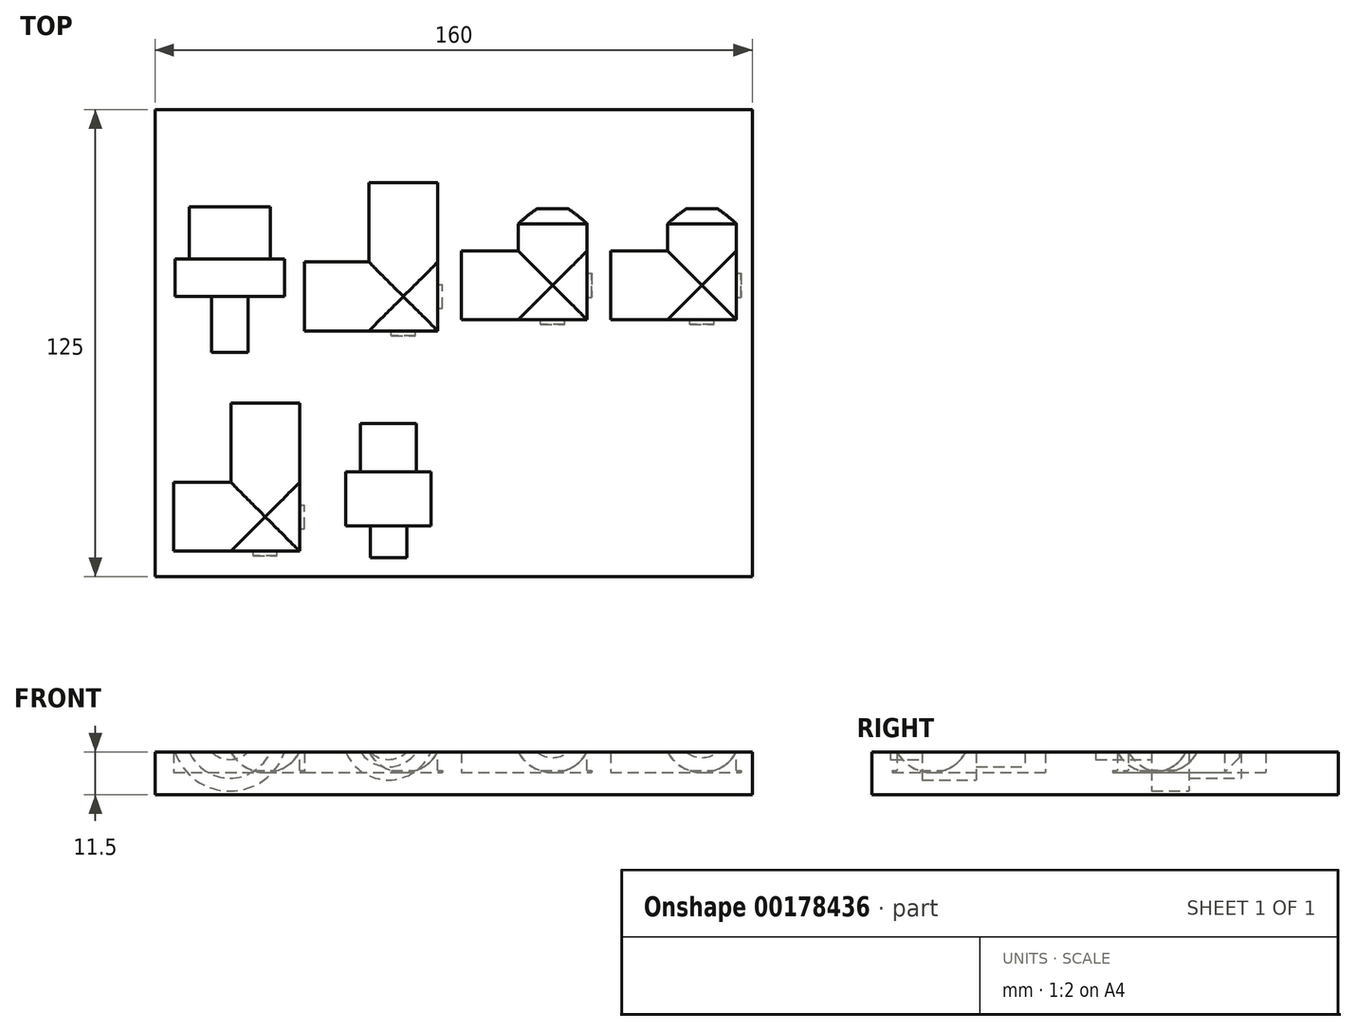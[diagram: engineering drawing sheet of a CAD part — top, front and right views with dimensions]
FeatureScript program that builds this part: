
annotation { "Feature Type Name" : "Feature", "Feature Type Description" : "" }
export const myFeature = defineFeature(function(context is Context, id is Id, definition is map)
    precondition{}
    {
        {
            var Q0;
            Q0=qCreatedBy(makeId("Top.planeOp"),FACE);
            var sketch = newSketch(context, id + "F0", { "sketchPlane" : qUnion([Q0])});
            skLineSegment(sketch, "E0.bottom", {"start": v(0, 0) * mm, "end": v(160, 0) * mm});
            skLineSegment(sketch, "E0.top", {"start": v(0, 125) * mm, "end": v(160, 125) * mm});
            skLineSegment(sketch, "E0.left", {"start": v(0, 0) * mm, "end": v(0, 125) * mm});
            skLineSegment(sketch, "E0.right", {"start": v(160, 0) * mm, "end": v(160, 125) * mm});
            skSolve(sketch);
        }
        {
            var Q0;
            Q0=makeQuery(id+"F0.imprint","IMPRINT",FACE,{"disambiguationData":[TD([[makeQuery(id+"F0.imprint","IMPRINT",EDGE,{"derivedFrom":sQuery(id+"F0.wireOp",EDGE,"E0.bottom")}),1.0]])]});
            extrude(context, id + "F1", {"entities" : qUnion([Q0]), "oppositeDirection" : true, "depth" : 16.5 * mm});
        }
        {
            var Q0;
            Q0=makeQuery(id+"F1.opExtrude","CAP_FACE",FACE,{"disambiguationData":[OSD([sQuery(id+"F0.wireOp",EDGE,"E0.bottom"),sQuery(id+"F0.wireOp",EDGE,"E0.top"),sQuery(id+"F0.wireOp",EDGE,"E0.left"),sQuery(id+"F0.wireOp",EDGE,"E0.right")])],"isStart":true});
            var sketch = newSketch(context, id + "F2", { "sketchPlane" : qUnion([Q0])});
            skLineSegment(sketch, "E1.bottom", {"start": v(0, 0) * mm, "end": v(20, 0) * mm, "construction": true});
            skLineSegment(sketch, "E1.top", {"start": v(0, 60) * mm, "end": v(20, 60) * mm, "construction": true});
            skLineSegment(sketch, "E1.left", {"start": v(0, 0) * mm, "end": v(0, 60) * mm, "construction": true});
            skLineSegment(sketch, "E1.right", {"start": v(20, 0) * mm, "end": v(20, 60) * mm, "construction": true});
            skLineSegment(sketch, "E2.bottom", {"start": v(20, 60) * mm, "end": v(27, 60) * mm});
            skLineSegment(sketch, "E2.left", {"start": v(20, 60) * mm, "end": v(20, 75) * mm});
            skLineSegment(sketch, "E2.right", {"start": v(27, 60) * mm, "end": v(27, 75) * mm});
            skLineSegment(sketch, "E3.bottom", {"start": v(27, 75) * mm, "end": v(35.5, 75) * mm});
            skLineSegment(sketch, "E3.top", {"start": v(32, 85) * mm, "end": v(35.5, 85) * mm});
            skLineSegment(sketch, "E3.left", {"start": v(20, 75) * mm, "end": v(20, 85) * mm});
            skLineSegment(sketch, "E3.right", {"start": v(35.5, 75) * mm, "end": v(35.5, 85) * mm});
            skLineSegment(sketch, "E4.top", {"start": v(24.5, 99) * mm, "end": v(32, 99) * mm});
            skLineSegment(sketch, "E4.left", {"start": v(20, 85) * mm, "end": v(20, 99) * mm});
            skLineSegment(sketch, "E4.right", {"start": v(32, 85) * mm, "end": v(32, 99) * mm});
            skLineSegment(sketch, "E5.top", {"start": v(20, 113) * mm, "end": v(24.5, 113) * mm});
            skLineSegment(sketch, "E5.left", {"start": v(20, 99) * mm, "end": v(20, 113) * mm});
            skLineSegment(sketch, "E5.right", {"start": v(24.5, 99) * mm, "end": v(24.5, 113) * mm});
            skSolve(sketch);
        }
        {
            var Q0;
            Q0=qSketchRegion(id+"F2",true);
            var Q1;
            Q1=sQuery(id+"F2.wireOp",EDGE,"E4.left");
            revolve(context, id + "F3", {"operationType" : NewBodyOperationType.REMOVE, "entities" : qUnion([Q0]), "axis" : qUnion([Q1]), "revolveType" : RevolveType.FULL, "oppositeDirection" : true});
        }
        {
            var Q0;
            Q0=makeQuery(id+"F1.opExtrude","CAP_FACE",FACE,{"disambiguationData":[OSD([sQuery(id+"F0.wireOp",EDGE,"E0.bottom"),sQuery(id+"F0.wireOp",EDGE,"E0.top"),sQuery(id+"F0.wireOp",EDGE,"E0.left"),sQuery(id+"F0.wireOp",EDGE,"E0.right")])],"isStart":true});
            var sketch = newSketch(context, id + "F4", { "sketchPlane" : qUnion([Q0])});
            skLineSegment(sketch, "E6.bottom", {"start": v(0, 0) * mm, "end": v(5, 0) * mm, "construction": true});
            skLineSegment(sketch, "E6.top", {"start": v(0, 16) * mm, "end": v(5, 16) * mm, "construction": true});
            skLineSegment(sketch, "E6.left", {"start": v(0, 0) * mm, "end": v(0, 16) * mm, "construction": true});
            skLineSegment(sketch, "E6.right", {"start": v(5, 0) * mm, "end": v(5, 16) * mm, "construction": true});
            skLineSegment(sketch, "E7.bottom", {"start": v(5, 16) * mm, "end": v(40, 16) * mm});
            skLineSegment(sketch, "E7.top", {"start": v(5, 5.5) * mm, "end": v(40, 5.5) * mm});
            skLineSegment(sketch, "E7.left", {"start": v(5, 16) * mm, "end": v(5, 5.5) * mm});
            skLineSegment(sketch, "E7.right", {"start": v(40, 16) * mm, "end": v(40, 5.5) * mm});
            skSolve(sketch);
        }
        {
            var Q0;
            Q0=makeQuery(id+"F4.imprint","IMPRINT",FACE,{"disambiguationData":[TD([[makeQuery(id+"F4.imprint","IMPRINT",EDGE,{"derivedFrom":sQuery(id+"F4.wireOp",EDGE,"E7.bottom")}),-1.0]])]});
            var Q1;
            Q1=sQuery(id+"F4.wireOp",EDGE,"E7.bottom");
            revolve(context, id + "F5", {"operationType" : NewBodyOperationType.REMOVE, "entities" : qUnion([Q0]), "axis" : qUnion([Q1]), "revolveType" : RevolveType.FULL, "oppositeDirection" : true});
        }
        {
            var Q0;
            Q0=makeQuery(id+"F1.opExtrude","CAP_FACE",FACE,{"disambiguationData":[OSD([sQuery(id+"F0.wireOp",EDGE,"E0.bottom"),sQuery(id+"F0.wireOp",EDGE,"E0.top"),sQuery(id+"F0.wireOp",EDGE,"E0.left"),sQuery(id+"F0.wireOp",EDGE,"E0.right")])],"isStart":true});
            var sketch = newSketch(context, id + "F6", { "sketchPlane" : qUnion([Q0])});
            skLineSegment(sketch, "E8.bottom", {"start": v(0, 0) * mm, "end": v(40, 0) * mm, "construction": true});
            skLineSegment(sketch, "E8.top", {"start": v(0, 75) * mm, "end": v(40, 75) * mm, "construction": true});
            skLineSegment(sketch, "E8.left", {"start": v(0, 0) * mm, "end": v(0, 75) * mm, "construction": true});
            skLineSegment(sketch, "E8.right", {"start": v(40, 0) * mm, "end": v(40, 75) * mm, "construction": true});
            skPoint(sketch, "E9.oppositeSnap0", {"position": v(31, 64.5) * mm});
            skLineSegment(sketch, "E9.bottom", {"start": v(40, 75) * mm, "end": v(77, 75) * mm});
            skLineSegment(sketch, "E9.top", {"start": v(40, 64.5) * mm, "end": v(77, 64.5) * mm});
            skLineSegment(sketch, "E9.left", {"start": v(40, 75) * mm, "end": v(40, 64.5) * mm});
            skLineSegment(sketch, "E9.right", {"start": v(77, 75) * mm, "end": v(77, 64.5) * mm});
            skSolve(sketch);
        }
        {
            var Q0;
            Q0=makeQuery(id+"F6.imprint","IMPRINT",FACE,{"disambiguationData":[TD([[makeQuery(id+"F6.imprint","IMPRINT",EDGE,{"derivedFrom":sQuery(id+"F6.wireOp",EDGE,"E9.bottom")}),-1.0]])]});
            var Q1;
            Q1=sQuery(id+"F6.wireOp",EDGE,"E9.bottom");
            revolve(context, id + "F7", {"operationType" : NewBodyOperationType.REMOVE, "entities" : qUnion([Q0]), "axis" : qUnion([Q1]), "revolveType" : RevolveType.FULL, "oppositeDirection" : true});
        }
        {
            var Q0;
            Q0=makeQuery(id+"F1.opExtrude","CAP_FACE",FACE,{"disambiguationData":[OSD([sQuery(id+"F0.wireOp",EDGE,"E0.bottom"),sQuery(id+"F0.wireOp",EDGE,"E0.top"),sQuery(id+"F0.wireOp",EDGE,"E0.left"),sQuery(id+"F0.wireOp",EDGE,"E0.right")])],"isStart":true});
            var sketch = newSketch(context, id + "F8", { "sketchPlane" : qUnion([Q0])});
            skLineSegment(sketch, "E10.bottom", {"start": v(77, 64.5) * mm, "end": v(66.5, 64.5) * mm});
            skLineSegment(sketch, "E10.top", {"start": v(77, 105.5) * mm, "end": v(66.5, 105.5) * mm});
            skLineSegment(sketch, "E10.left", {"start": v(77, 64.5) * mm, "end": v(77, 105.5) * mm});
            skLineSegment(sketch, "E10.right", {"start": v(66.5, 64.5) * mm, "end": v(66.5, 105.5) * mm});
            skSolve(sketch);
        }
        {
            var Q0;
            {var subQ0=sQuery(id+"F8.wireOp",EDGE,"E10.top");Q0=makeQuery(id+"F8.imprint","IMPRINT",FACE,{"disambiguationData":[TD([[makeQuery(id+"F8.imprint","IMPRINT",EDGE,{"derivedFrom":subQ0}),1.0]])]});}
            var Q1;
            {var subQ0=sQuery(id+"F8.wireOp",EDGE,"E10.bottom");Q1=makeQuery(id+"F8.imprint","IMPRINT",FACE,{"disambiguationData":[TD([[makeQuery(id+"F8.imprint","IMPRINT",EDGE,{"derivedFrom":subQ0}),-1.0]])]});}
            var Q2;
            Q2=sQuery(id+"F8.wireOp",EDGE,"E10.right");
            revolve(context, id + "F9", {"operationType" : NewBodyOperationType.REMOVE, "entities" : qUnion([Q0, Q1]), "axis" : qUnion([Q2]), "revolveType" : RevolveType.FULL, "oppositeDirection" : true});
        }
        {
            var Q0;
            Q0=makeQuery(id+"F1.opExtrude","CAP_FACE",FACE,{"disambiguationData":[OSD([sQuery(id+"F0.wireOp",EDGE,"E0.bottom"),sQuery(id+"F0.wireOp",EDGE,"E0.top"),sQuery(id+"F0.wireOp",EDGE,"E0.left"),sQuery(id+"F0.wireOp",EDGE,"E0.right")])],"isStart":true});
            var sketch = newSketch(context, id + "F10", { "sketchPlane" : qUnion([Q0])});
            skLineSegment(sketch, "E11.bottom", {"start": v(77, 64.5) * mm, "end": v(82, 64.5) * mm, "construction": true});
            skLineSegment(sketch, "E11.top", {"start": v(77, 67.5) * mm, "end": v(82, 67.5) * mm, "construction": true});
            skLineSegment(sketch, "E11.left", {"start": v(77, 64.5) * mm, "end": v(77, 67.5) * mm, "construction": true});
            skLineSegment(sketch, "E11.right", {"start": v(82, 64.5) * mm, "end": v(82, 67.5) * mm, "construction": true});
            skLineSegment(sketch, "E12.bottom", {"start": v(82, 67.5) * mm, "end": v(117, 67.5) * mm});
            skLineSegment(sketch, "E12.top", {"start": v(82, 78) * mm, "end": v(117, 78) * mm});
            skLineSegment(sketch, "E12.left", {"start": v(82, 67.5) * mm, "end": v(82, 78) * mm});
            skLineSegment(sketch, "E12.right", {"start": v(117, 67.5) * mm, "end": v(117, 78) * mm});
            skLineSegment(sketch, "E13", {"start": v(117, 67.5) * mm, "end": v(122, 67.5) * mm, "construction": true});
            skLineSegment(sketch, "E14.bottom", {"start": v(122, 67.5) * mm, "end": v(157, 67.5) * mm});
            skLineSegment(sketch, "E14.top", {"start": v(122, 78) * mm, "end": v(157, 78) * mm});
            skLineSegment(sketch, "E14.left", {"start": v(122, 67.5) * mm, "end": v(122, 78) * mm});
            skLineSegment(sketch, "E14.right", {"start": v(157, 67.5) * mm, "end": v(157, 78) * mm});
            skSolve(sketch);
        }
        {
            var Q0;
            Q0=makeQuery(id+"F10.imprint","IMPRINT",FACE,{"disambiguationData":[TD([[makeQuery(id+"F10.imprint","IMPRINT",EDGE,{"derivedFrom":sQuery(id+"F10.wireOp",EDGE,"E12.bottom")}),1.0]])]});
            var Q1;
            Q1=makeQuery(id+"F10.imprint","IMPRINT",FACE,{"disambiguationData":[TD([[makeQuery(id+"F10.imprint","IMPRINT",EDGE,{"derivedFrom":sQuery(id+"F10.wireOp",EDGE,"E14.bottom")}),1.0]])]});
            var Q2;
            Q2=sQuery(id+"F10.wireOp",EDGE,"E12.top");
            revolve(context, id + "F11", {"operationType" : NewBodyOperationType.REMOVE, "entities" : qUnion([Q0, Q1]), "axis" : qUnion([Q2]), "revolveType" : RevolveType.FULL, "oppositeDirection" : true});
        }
        {
            var Q0;
            Q0=makeQuery(id+"F1.opExtrude","CAP_FACE",FACE,{"disambiguationData":[OSD([sQuery(id+"F0.wireOp",EDGE,"E0.bottom"),sQuery(id+"F0.wireOp",EDGE,"E0.top"),sQuery(id+"F0.wireOp",EDGE,"E0.left"),sQuery(id+"F0.wireOp",EDGE,"E0.right")])],"isStart":true});
            var sketch = newSketch(context, id + "F12", { "sketchPlane" : qUnion([Q0])});
            skLineSegment(sketch, "E15.bottom", {"start": v(117, 67.5) * mm, "end": v(106.5, 67.5) * mm});
            skLineSegment(sketch, "E15.top", {"start": v(113, 98.5) * mm, "end": v(106.5, 98.5) * mm});
            skLineSegment(sketch, "E15.left", {"start": v(117, 67.5) * mm, "end": v(117, 94.5) * mm});
            skLineSegment(sketch, "E15.right", {"start": v(106.5, 67.5) * mm, "end": v(106.5, 98.5) * mm});
            skLineSegment(sketch, "E16", {"start": v(117, 67.5) * mm, "end": v(117, 94.5) * mm, "construction": true});
            skLineSegment(sketch, "E17", {"start": v(117, 94.5) * mm, "end": v(113, 98.5) * mm});
            skSolve(sketch);
        }
        {
            var Q0;
            {var subQ5=sQuery(id+"F12.wireOp",EDGE,"E15.top");Q0=makeQuery(id+"F12.imprint","IMPRINT",FACE,{"disambiguationData":[TD([[makeQuery(id+"F12.imprint","IMPRINT",EDGE,{"derivedFrom":subQ5}),1.0]])]});}
            var Q1;
            {var subQ0=sQuery(id+"F12.wireOp",EDGE,"E15.bottom");Q1=makeQuery(id+"F12.imprint","IMPRINT",FACE,{"disambiguationData":[TD([[makeQuery(id+"F12.imprint","IMPRINT",EDGE,{"derivedFrom":subQ0}),-1.0]])]});}
            var Q2;
            Q2=sQuery(id+"F12.wireOp",EDGE,"E15.right");
            revolve(context, id + "F13", {"operationType" : NewBodyOperationType.REMOVE, "entities" : qUnion([Q0, Q1]), "axis" : qUnion([Q2]), "revolveType" : RevolveType.FULL, "oppositeDirection" : true});
        }
        {
            var Q0;
            Q0=makeQuery(id+"F1.opExtrude","CAP_FACE",FACE,{"disambiguationData":[OSD([sQuery(id+"F0.wireOp",EDGE,"E0.bottom"),sQuery(id+"F0.wireOp",EDGE,"E0.top"),sQuery(id+"F0.wireOp",EDGE,"E0.left"),sQuery(id+"F0.wireOp",EDGE,"E0.right")])],"isStart":true});
            var sketch = newSketch(context, id + "F14", { "sketchPlane" : qUnion([Q0])});
            skLineSegment(sketch, "E18.bottom", {"start": v(157, 67.5) * mm, "end": v(146.5, 67.5) * mm});
            skLineSegment(sketch, "E18.top", {"start": v(153, 98.5) * mm, "end": v(146.5, 98.5) * mm});
            skLineSegment(sketch, "E18.left", {"start": v(157, 67.5) * mm, "end": v(157, 94.5) * mm});
            skLineSegment(sketch, "E18.right", {"start": v(146.5, 67.5) * mm, "end": v(146.5, 98.5) * mm});
            skLineSegment(sketch, "E19", {"start": v(157, 67.5) * mm, "end": v(157, 94.5) * mm, "construction": true});
            skLineSegment(sketch, "E20", {"start": v(157, 94.5) * mm, "end": v(153, 98.5) * mm});
            skSolve(sketch);
        }
        {
            var Q0;
            {var subQ2=sQuery(id+"F14.wireOp",EDGE,"E18.top");Q0=makeQuery(id+"F14.imprint","IMPRINT",FACE,{"disambiguationData":[TD([[makeQuery(id+"F14.imprint","IMPRINT",EDGE,{"derivedFrom":subQ2}),1.0]])]});}
            var Q1;
            {var subQ0=sQuery(id+"F14.wireOp",EDGE,"E18.bottom");Q1=makeQuery(id+"F14.imprint","IMPRINT",FACE,{"disambiguationData":[TD([[makeQuery(id+"F14.imprint","IMPRINT",EDGE,{"derivedFrom":subQ0}),-1.0]])]});}
            var Q2;
            Q2=sQuery(id+"F14.wireOp",EDGE,"E18.right");
            revolve(context, id + "F15", {"operationType" : NewBodyOperationType.REMOVE, "entities" : qUnion([Q0, Q1]), "axis" : qUnion([Q2]), "revolveType" : RevolveType.FULL, "oppositeDirection" : true});
        }
        {
            var Q0;
            Q0=makeQuery(id+"F1.opExtrude","CAP_FACE",FACE,{"disambiguationData":[OSD([sQuery(id+"F0.wireOp",EDGE,"E0.bottom"),sQuery(id+"F0.wireOp",EDGE,"E0.top"),sQuery(id+"F0.wireOp",EDGE,"E0.left"),sQuery(id+"F0.wireOp",EDGE,"E0.right")])],"isStart":true});
            var sketch = newSketch(context, id + "F16", { "sketchPlane" : qUnion([Q0])});
            skLineSegment(sketch, "E21.bottom", {"start": v(40, 5.5) * mm, "end": v(29.5, 5.5) * mm});
            skLineSegment(sketch, "E21.top", {"start": v(40, 46.5) * mm, "end": v(29.5, 46.5) * mm});
            skLineSegment(sketch, "E21.left", {"start": v(40, 5.5) * mm, "end": v(40, 46.5) * mm});
            skLineSegment(sketch, "E21.right", {"start": v(29.5, 5.5) * mm, "end": v(29.5, 46.5) * mm});
            skSolve(sketch);
        }
        {
            var Q0;
            {var subQ0=sQuery(id+"F16.wireOp",EDGE,"E21.top");Q0=makeQuery(id+"F16.imprint","IMPRINT",FACE,{"disambiguationData":[TD([[makeQuery(id+"F16.imprint","IMPRINT",EDGE,{"derivedFrom":subQ0}),1.0]])]});}
            var Q1;
            {var subQ0=sQuery(id+"F16.wireOp",EDGE,"E21.bottom");Q1=makeQuery(id+"F16.imprint","IMPRINT",FACE,{"disambiguationData":[TD([[makeQuery(id+"F16.imprint","IMPRINT",EDGE,{"derivedFrom":subQ0}),-1.0]])]});}
            var Q2;
            Q2=sQuery(id+"F16.wireOp",EDGE,"E21.right");
            revolve(context, id + "F17", {"operationType" : NewBodyOperationType.REMOVE, "entities" : qUnion([Q0, Q1]), "axis" : qUnion([Q2]), "revolveType" : RevolveType.FULL, "oppositeDirection" : true});
        }
        {
            var Q0;
            Q0=makeQuery(id+"F1.opExtrude","CAP_FACE",FACE,{"disambiguationData":[OSD([sQuery(id+"F0.wireOp",EDGE,"E0.bottom"),sQuery(id+"F0.wireOp",EDGE,"E0.top"),sQuery(id+"F0.wireOp",EDGE,"E0.left"),sQuery(id+"F0.wireOp",EDGE,"E0.right")])],"isStart":true});
            var sketch = newSketch(context, id + "F18", { "sketchPlane" : qUnion([Q0])});
            skLineSegment(sketch, "E22.bottom", {"start": v(0, 0) * mm, "end": v(62.5, 0) * mm, "construction": true});
            skLineSegment(sketch, "E22.top", {"start": v(0, 5) * mm, "end": v(62.5, 5) * mm, "construction": true});
            skLineSegment(sketch, "E22.left", {"start": v(0, 0) * mm, "end": v(0, 5) * mm, "construction": true});
            skLineSegment(sketch, "E22.right", {"start": v(62.5, 0) * mm, "end": v(62.5, 5) * mm, "construction": true});
            skLineSegment(sketch, "E23.bottom", {"start": v(62.5, 5) * mm, "end": v(69.5, 5) * mm});
            skLineSegment(sketch, "E23.left", {"start": v(62.5, 5) * mm, "end": v(62.5, 13.5) * mm});
            skLineSegment(sketch, "E23.right", {"start": v(69.5, 5) * mm, "end": v(69.5, 13.5) * mm});
            skLineSegment(sketch, "E24.bottom", {"start": v(69.5, 13.5) * mm, "end": v(75, 13.5) * mm});
            skLineSegment(sketch, "E24.top", {"start": v(71.5, 28) * mm, "end": v(75, 28) * mm});
            skLineSegment(sketch, "E24.left", {"start": v(62.5, 13.5) * mm, "end": v(62.5, 28) * mm});
            skLineSegment(sketch, "E24.right", {"start": v(75, 13.5) * mm, "end": v(75, 28) * mm});
            skLineSegment(sketch, "E25.top", {"start": v(62.5, 41) * mm, "end": v(71.5, 41) * mm});
            skLineSegment(sketch, "E25.left", {"start": v(62.5, 28) * mm, "end": v(62.5, 41) * mm});
            skLineSegment(sketch, "E25.right", {"start": v(71.5, 28) * mm, "end": v(71.5, 41) * mm});
            skSolve(sketch);
        }
        {
            var Q0;
            Q0=makeQuery(id+"F18.imprint","IMPRINT",FACE,{"disambiguationData":[TD([[makeQuery(id+"F18.imprint","IMPRINT",EDGE,{"derivedFrom":sQuery(id+"F18.wireOp",EDGE,"E23.bottom")}),1.0]])]});
            var Q1;
            Q1=sQuery(id+"F18.wireOp",EDGE,"E24.left");
            revolve(context, id + "F19", {"operationType" : NewBodyOperationType.REMOVE, "entities" : qUnion([Q0]), "axis" : qUnion([Q1]), "revolveType" : RevolveType.FULL, "oppositeDirection" : true});
        }
        {
            var Q0;
            Q0=makeQuery(id+"F1.opExtrude","SWEPT_FACE",FACE,{"disambiguationData":[OSD([sQuery(id+"F0.wireOp",EDGE,"E0.bottom")])]});
            var sketch = newSketch(context, id + "F20", { "sketchPlane" : qUnion([Q0])});
            skLineSegment(sketch, "E26.bottom", {"start": v(0, 0) * mm, "end": v(160, 0) * mm});
            skLineSegment(sketch, "E26.top", {"start": v(0, -5) * mm, "end": v(160, -5) * mm});
            skLineSegment(sketch, "E26.left", {"start": v(0, 0) * mm, "end": v(0, -5) * mm});
            skLineSegment(sketch, "E26.right", {"start": v(160, 0) * mm, "end": v(160, -5) * mm});
            skSolve(sketch);
        }
        {
            var Q0;
            Q0=makeQuery(id+"F20.imprint","IMPRINT",FACE,{"disambiguationData":[TD([[makeQuery(id+"F20.imprint","IMPRINT",EDGE,{"derivedFrom":sQuery(id+"F20.wireOp",EDGE,"E26.bottom")}),-1.0]])]});
            extrude(context, id + "F21", {"entities" : qUnion([Q0]), "operationType" : NewBodyOperationType.REMOVE, "oppositeDirection" : true, "depth" : 160 * mm});
        }
        {
            var Q0;
            Q0=makeQuery(id+"F21.boolean.opBoolean","COPY",FACE,{"derivedFrom":makeQuery(id+"F21.opExtrude","SWEPT_FACE",FACE,{"disambiguationData":[OSD([sQuery(id+"F20.wireOp",EDGE,"E26.top")])]})});
            var sketch = newSketch(context, id + "F22", { "sketchPlane" : qUnion([Q0])});
            skLineSegment(sketch, "E27.bottom", {"start": v(20.27, 6.77) * mm, "end": v(38.73, 6.77) * mm});
            skLineSegment(sketch, "E27.top", {"start": v(20.27, 5.5) * mm, "end": v(38.73, 5.5) * mm});
            skLineSegment(sketch, "E27.left", {"start": v(20.27, 6.77) * mm, "end": v(20.27, 5.5) * mm});
            skLineSegment(sketch, "E27.right", {"start": v(38.73, 6.77) * mm, "end": v(38.73, 5.5) * mm});
            skLineSegment(sketch, "E28.bottom", {"start": v(40, 6.77) * mm, "end": v(38.73, 6.77) * mm});
            skLineSegment(sketch, "E28.top", {"start": v(40, 25.23) * mm, "end": v(38.73, 25.23) * mm});
            skLineSegment(sketch, "E28.left", {"start": v(40, 6.77) * mm, "end": v(40, 25.23) * mm});
            skLineSegment(sketch, "E28.right", {"start": v(38.73, 6.77) * mm, "end": v(38.73, 25.23) * mm});
            skLineSegment(sketch, "E29.bottom", {"start": v(57.27, 65.77) * mm, "end": v(75.73, 65.77) * mm});
            skLineSegment(sketch, "E29.top", {"start": v(57.27, 64.5) * mm, "end": v(75.73, 64.5) * mm});
            skLineSegment(sketch, "E29.left", {"start": v(57.27, 65.77) * mm, "end": v(57.27, 64.5) * mm});
            skLineSegment(sketch, "E29.right", {"start": v(75.73, 65.77) * mm, "end": v(75.73, 64.5) * mm});
            skLineSegment(sketch, "E30.bottom", {"start": v(77, 65.77) * mm, "end": v(75.73, 65.77) * mm});
            skLineSegment(sketch, "E30.top", {"start": v(77, 84.23) * mm, "end": v(75.73, 84.23) * mm});
            skLineSegment(sketch, "E30.left", {"start": v(77, 65.77) * mm, "end": v(77, 84.23) * mm});
            skLineSegment(sketch, "E30.right", {"start": v(75.73, 65.77) * mm, "end": v(75.73, 84.23) * mm});
            skLineSegment(sketch, "E31.bottom", {"start": v(97.27, 68.77) * mm, "end": v(115.73, 68.77) * mm});
            skLineSegment(sketch, "E31.top", {"start": v(97.27, 67.5) * mm, "end": v(115.73, 67.5) * mm});
            skLineSegment(sketch, "E31.left", {"start": v(97.27, 68.77) * mm, "end": v(97.27, 67.5) * mm});
            skLineSegment(sketch, "E31.right", {"start": v(115.73, 68.77) * mm, "end": v(115.73, 67.5) * mm});
            skLineSegment(sketch, "E32.bottom", {"start": v(117, 68.77) * mm, "end": v(115.73, 68.77) * mm});
            skLineSegment(sketch, "E32.top", {"start": v(117, 87.23) * mm, "end": v(115.73, 87.23) * mm});
            skLineSegment(sketch, "E32.left", {"start": v(117, 68.77) * mm, "end": v(117, 87.23) * mm});
            skLineSegment(sketch, "E32.right", {"start": v(115.73, 68.77) * mm, "end": v(115.73, 87.23) * mm});
            skLineSegment(sketch, "E33.bottom", {"start": v(137.27, 68.77) * mm, "end": v(155.73, 68.77) * mm});
            skLineSegment(sketch, "E33.top", {"start": v(137.27, 67.5) * mm, "end": v(155.73, 67.5) * mm});
            skLineSegment(sketch, "E33.left", {"start": v(137.27, 68.77) * mm, "end": v(137.27, 67.5) * mm});
            skLineSegment(sketch, "E33.right", {"start": v(155.73, 68.77) * mm, "end": v(155.73, 67.5) * mm});
            skLineSegment(sketch, "E34.bottom", {"start": v(157, 68.77) * mm, "end": v(155.73, 68.77) * mm});
            skLineSegment(sketch, "E34.top", {"start": v(157, 87.23) * mm, "end": v(155.73, 87.23) * mm});
            skLineSegment(sketch, "E34.left", {"start": v(157, 68.77) * mm, "end": v(157, 87.23) * mm});
            skLineSegment(sketch, "E34.right", {"start": v(155.73, 68.77) * mm, "end": v(155.73, 87.23) * mm});
            skSolve(sketch);
        }
        {
            var Q0;
            Q0 = qSketchRegion(id + "F22", true);
            extrude(context, id + "F23", {"entities" : qUnion([Q0]), "operationType" : NewBodyOperationType.ADD, "oppositeDirection" : true, "depth" : 5 * mm});
        }
    });
